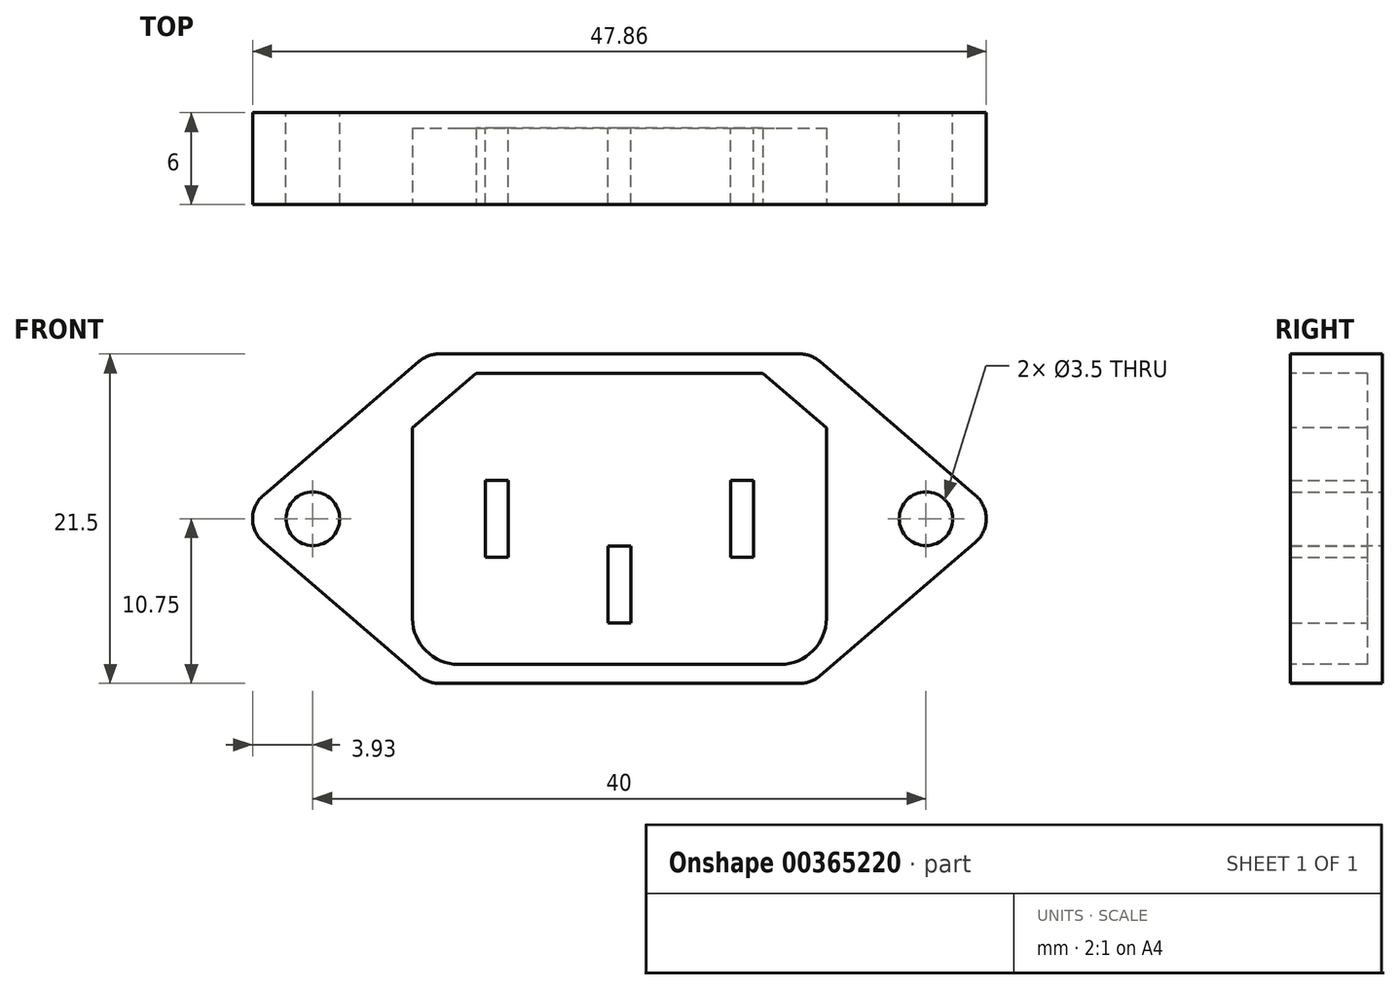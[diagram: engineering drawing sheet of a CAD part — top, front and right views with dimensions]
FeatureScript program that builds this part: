
annotation { "Feature Type Name" : "Feature", "Feature Type Description" : "" }
export const myFeature = defineFeature(function(context is Context, id is Id, definition is map)
    precondition{}
    {
        {
            var Q0;
            Q0=qCreatedBy(makeId("Front.planeOp"),FACE);
            var sketch = newSketch(context, id + "F0", { "sketchPlane" : qUnion([Q0])});
            skLineSegment(sketch, "E0", {"start": v(0, 0) * mm, "end": v(20, 0) * mm, "construction": true});
            skCircle(sketch, "E1", {"center": v(20, 0) * mm, "radius": 1.75 * mm});
            skLineSegment(sketch, "E2", {"start": v(0, 0) * mm, "end": v(0, 10.75) * mm, "construction": true});
            skLineSegment(sketch, "E3", {"start": v(0, 10.75) * mm, "end": v(25, 10.75) * mm, "construction": true});
            skLineSegment(sketch, "E4", {"start": v(25, 10.75) * mm, "end": v(25, 0) * mm, "construction": true});
            skLineSegment(sketch, "E5", {"start": v(0, 10.75) * mm, "end": v(12.5, 10.75) * mm, "construction": true});
            skLineSegment(sketch, "E6", {"start": v(13.06, 10.27) * mm, "end": v(23.24, 1.52) * mm});
            skLineSegment(sketch, "E7", {"start": v(11.76, 10.75) * mm, "end": v(0, 10.75) * mm});
            skPoint(sketch, "E8.visualSharp", {"position": v(12.5, 10.75) * mm});
            skArc(sketch, "E8.filletArc", {"start": v(13.06, 10.27) * mm, "mid": v(12.45, 10.63) * mm, "end": v(11.76, 10.75) * mm});
            skLineSegment(sketch, "E9.MirrorCS", {"start": v(11.76, -10.75) * mm, "end": v(0, -10.75) * mm});
            skLineSegment(sketch, "E10.MirrorCS", {"start": v(13.06, -10.27) * mm, "end": v(23.24, -1.52) * mm});
            skArc(sketch, "E11.MirrorCS", {"start": v(13.06, -10.27) * mm, "mid": v(12.45, -10.63) * mm, "end": v(11.76, -10.75) * mm});
            skPoint(sketch, "E12.visualSharp", {"position": v(25, 0) * mm});
            skArc(sketch, "E12.filletArc", {"start": v(23.24, -1.52) * mm, "mid": v(23.93, 0) * mm, "end": v(23.24, 1.52) * mm});
            skLineSegment(sketch, "E13.MirrorCS", {"start": v(-11.76, -10.75) * mm, "end": v(0, -10.75) * mm});
            skArc(sketch, "E14.MirrorCS", {"start": v(-13.06, -10.27) * mm, "mid": v(-12.45, -10.63) * mm, "end": v(-11.76, -10.75) * mm});
            skLineSegment(sketch, "E15.MirrorCS", {"start": v(-13.06, -10.27) * mm, "end": v(-23.24, -1.52) * mm});
            skCircle(sketch, "E16.MirrorC", {"center": v(-20, 0) * mm, "radius": 1.75 * mm});
            skLineSegment(sketch, "E17.MirrorCS", {"start": v(-13.06, 10.27) * mm, "end": v(-23.24, 1.52) * mm});
            skLineSegment(sketch, "E18.MirrorCS", {"start": v(-11.76, 10.75) * mm, "end": v(0, 10.75) * mm});
            skArc(sketch, "E19.MirrorCS", {"start": v(-13.06, 10.27) * mm, "mid": v(-12.45, 10.63) * mm, "end": v(-11.76, 10.75) * mm});
            skArc(sketch, "E20.MirrorCS", {"start": v(-23.24, -1.52) * mm, "mid": v(-23.93, 0) * mm, "end": v(-23.24, 1.52) * mm});
            skSolve(sketch);
        }
        {
            var Q0;
            Q0=makeQuery(id+"F0.imprint","IMPRINT",FACE,{"disambiguationData":[TD([[makeQuery(id+"F0.imprint","IMPRINT",EDGE,{"derivedFrom":sQuery(id+"F0.wireOp",EDGE,"E1")}),-1.0]])]});
            extrude(context, id + "F1", {"entities" : qUnion([Q0]), "depth" : 6 * mm});
        }
        {
            var Q0;
            Q0=makeQuery(id+"F1.opExtrude","CAP_FACE",FACE,{"disambiguationData":[OSD([sQuery(id+"F0.wireOp",EDGE,"E1"),sQuery(id+"F0.wireOp",EDGE,"E6"),sQuery(id+"F0.wireOp",EDGE,"E7"),sQuery(id+"F0.wireOp",EDGE,"E8.filletArc"),sQuery(id+"F0.wireOp",EDGE,"E9.MirrorCS"),sQuery(id+"F0.wireOp",EDGE,"E10.MirrorCS"),sQuery(id+"F0.wireOp",EDGE,"E11.MirrorCS"),sQuery(id+"F0.wireOp",EDGE,"E12.filletArc"),sQuery(id+"F0.wireOp",EDGE,"E13.MirrorCS"),sQuery(id+"F0.wireOp",EDGE,"E14.MirrorCS"),sQuery(id+"F0.wireOp",EDGE,"E15.MirrorCS"),sQuery(id+"F0.wireOp",EDGE,"E16.MirrorC"),sQuery(id+"F0.wireOp",EDGE,"E17.MirrorCS"),sQuery(id+"F0.wireOp",EDGE,"E18.MirrorCS"),sQuery(id+"F0.wireOp",EDGE,"E19.MirrorCS"),sQuery(id+"F0.wireOp",EDGE,"E20.MirrorCS")])],"isStart":false});
            var sketch = newSketch(context, id + "F2", { "sketchPlane" : qUnion([Q0])});
            skLineSegment(sketch, "E21.bottom", {"start": v(10.5, -9.5) * mm, "end": v(-10.5, -9.5) * mm, "construction": true});
            skLineSegment(sketch, "E21.top", {"start": v(13.5, 9.5) * mm, "end": v(-13.5, 9.5) * mm, "construction": true});
            skLineSegment(sketch, "E21.left", {"start": v(13.5, -6.5) * mm, "end": v(13.5, 9.5) * mm, "construction": true});
            skLineSegment(sketch, "E21.right", {"start": v(-13.5, -6.5) * mm, "end": v(-13.5, 9.5) * mm, "construction": true});
            skPoint(sketch, "E21.middle", {"position": v(0, 0) * mm});
            skPoint(sketch, "E22.visualSharp", {"position": v(-13.5, -9.5) * mm});
            skArc(sketch, "E22.filletArc", {"start": v(-13.5, -6.5) * mm, "mid": v(-12.62, -8.62) * mm, "end": v(-10.5, -9.5) * mm});
            skPoint(sketch, "E23.visualSharp", {"position": v(13.5, -9.5) * mm});
            skArc(sketch, "E23.filletArc", {"start": v(10.5, -9.5) * mm, "mid": v(12.62, -8.62) * mm, "end": v(13.5, -6.5) * mm});
            skLineSegment(sketch, "E24.0", {"start": v(-13.06, 10.27) * mm, "end": v(-23.24, 1.52) * mm, "construction": true});
            skLineSegment(sketch, "E25.0", {"start": v(13.06, 10.27) * mm, "end": v(23.24, 1.52) * mm, "construction": true});
            skLineSegment(sketch, "E26.0", {"start": v(-11.1, 8) * mm, "end": v(-21.28, -0.76) * mm, "construction": true});
            skLineSegment(sketch, "E27.0", {"start": v(11.1, 8) * mm, "end": v(21.28, -0.76) * mm, "construction": true});
            skLineSegment(sketch, "E28", {"start": v(-13.5, 5.93) * mm, "end": v(-9.35, 9.5) * mm, "construction": true});
            skLineSegment(sketch, "E29", {"start": v(13.5, 5.93) * mm, "end": v(9.35, 9.5) * mm, "construction": true});
            skLineSegment(sketch, "E30", {"start": v(-13.5, 5.93) * mm, "end": v(-13.5, -6.5) * mm});
            skLineSegment(sketch, "E31", {"start": v(-10.5, -9.5) * mm, "end": v(10.5, -9.5) * mm});
            skLineSegment(sketch, "E32", {"start": v(13.5, -6.5) * mm, "end": v(13.5, 5.93) * mm});
            skLineSegment(sketch, "E33", {"start": v(9.35, 9.5) * mm, "end": v(-9.35, 9.5) * mm});
            skLineSegment(sketch, "E34", {"start": v(-13.5, 5.93) * mm, "end": v(-9.35, 9.5) * mm});
            skLineSegment(sketch, "E35", {"start": v(9.35, 9.5) * mm, "end": v(13.5, 5.93) * mm});
            skSolve(sketch);
        }
        {
            var Q0;
            Q0 = qSketchRegion(id + "F2", true);
            extrude(context, id + "F3", {"entities" : qUnion([Q0]), "operationType" : NewBodyOperationType.REMOVE, "oppositeDirection" : true, "depth" : 5 * mm});
        }
        {
            var Q0;
            Q0=makeQuery(id+"F3.boolean.opBoolean","COPY",FACE,{"derivedFrom":makeQuery(id+"F3.opExtrude","CAP_FACE",FACE,{"disambiguationData":[OSD([sQuery(id+"F2.wireOp",EDGE,"E22.filletArc"),sQuery(id+"F2.wireOp",EDGE,"E23.filletArc"),sQuery(id+"F2.wireOp",EDGE,"E30"),sQuery(id+"F2.wireOp",EDGE,"E31"),sQuery(id+"F2.wireOp",EDGE,"E32"),sQuery(id+"F2.wireOp",EDGE,"E33"),sQuery(id+"F2.wireOp",EDGE,"E34"),sQuery(id+"F2.wireOp",EDGE,"E35")])],"isStart":false})});
            var sketch = newSketch(context, id + "F4", { "sketchPlane" : qUnion([Q0])});
            skLineSegment(sketch, "E36.bottom", {"start": v(0.75, -1.8) * mm, "end": v(-0.75, -1.8) * mm});
            skLineSegment(sketch, "E36.top", {"start": v(0.75, -6.8) * mm, "end": v(-0.75, -6.8) * mm});
            skLineSegment(sketch, "E36.left", {"start": v(0.75, -1.8) * mm, "end": v(0.75, -6.8) * mm});
            skLineSegment(sketch, "E36.right", {"start": v(-0.75, -1.8) * mm, "end": v(-0.75, -6.8) * mm});
            skPoint(sketch, "E36.middle", {"position": v(0, -4.3) * mm});
            skLineSegment(sketch, "E37.bottom", {"start": v(-7.25, 2.5) * mm, "end": v(-8.75, 2.5) * mm});
            skLineSegment(sketch, "E37.top", {"start": v(-7.25, -2.5) * mm, "end": v(-8.75, -2.5) * mm});
            skLineSegment(sketch, "E37.left", {"start": v(-7.25, 2.5) * mm, "end": v(-7.25, -2.5) * mm});
            skLineSegment(sketch, "E37.right", {"start": v(-8.75, 2.5) * mm, "end": v(-8.75, -2.5) * mm});
            skPoint(sketch, "E37.middle", {"position": v(-8, 0) * mm});
            skLineSegment(sketch, "E38.MirrorCS", {"start": v(7.25, 2.5) * mm, "end": v(7.25, -2.5) * mm});
            skLineSegment(sketch, "E39.MirrorCS", {"start": v(7.25, 2.5) * mm, "end": v(8.75, 2.5) * mm});
            skLineSegment(sketch, "E40.MirrorCS", {"start": v(8.75, 2.5) * mm, "end": v(8.75, -2.5) * mm});
            skLineSegment(sketch, "E41.MirrorCS", {"start": v(7.25, -2.5) * mm, "end": v(8.75, -2.5) * mm});
            skSolve(sketch);
        }
        {
            var Q0;
            Q0 = qSketchRegion(id + "F4", true);
            extrude(context, id + "F5", {"entities" : qUnion([Q0]), "operationType" : NewBodyOperationType.ADD, "depth" : 5 * mm});
        }
    });
